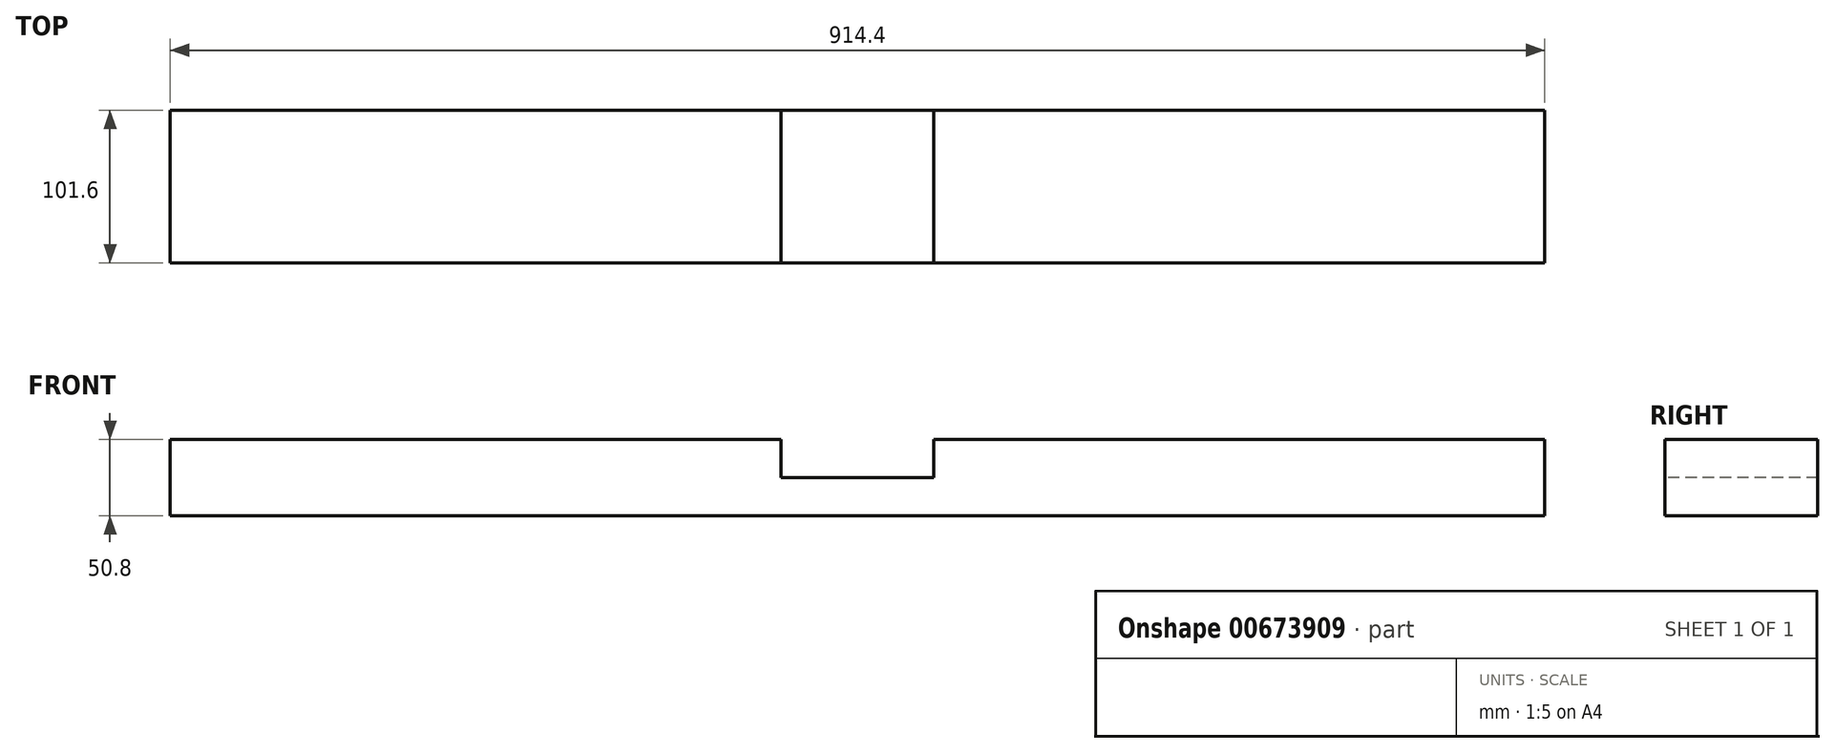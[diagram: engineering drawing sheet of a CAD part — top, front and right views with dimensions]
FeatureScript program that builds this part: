
annotation { "Feature Type Name" : "Feature", "Feature Type Description" : "" }
export const myFeature = defineFeature(function(context is Context, id is Id, definition is map)
    precondition{}
    {
        {
            var Q0;
            Q0=qCreatedBy(makeId("Front.planeOp"),FACE);
            var sketch = newSketch(context, id + "F0", { "sketchPlane" : qUnion([Q0])});
            skLineSegment(sketch, "E0.bottom", {"start": v(457.2, 25.4) * mm, "end": v(-457.2, 25.4) * mm});
            skLineSegment(sketch, "E0.top", {"start": v(457.2, -25.4) * mm, "end": v(-457.2, -25.4) * mm});
            skLineSegment(sketch, "E0.left", {"start": v(457.2, 25.4) * mm, "end": v(457.2, -25.4) * mm});
            skLineSegment(sketch, "E0.right", {"start": v(-457.2, 25.4) * mm, "end": v(-457.2, -25.4) * mm});
            skPoint(sketch, "E0.middle", {"position": v(0, 0) * mm});
            skSolve(sketch);
        }
        {
            var Q0;
            Q0 = qSketchRegion(id + "F0", true);
            extrude(context, id + "F1", {"entities" : qUnion([Q0]), "endBound" : BoundingType.SYMMETRIC, "depth" : 101.6 * mm, "offsetDistance" : 25.4 * mm});
        }
        {
            var Q0;
            Q0=makeQuery(id+"F1.opExtrude","SWEPT_FACE",FACE,{"disambiguationData":[OSD([sQuery(id+"F0.wireOp",EDGE,"E0.bottom")])]});
            var sketch = newSketch(context, id + "F2", { "sketchPlane" : qUnion([Q0])});
            skLineSegment(sketch, "E1.bottom", {"start": v(50.8, 50.8) * mm, "end": v(-50.8, 50.8) * mm});
            skLineSegment(sketch, "E1.top", {"start": v(50.8, -50.8) * mm, "end": v(-50.8, -50.8) * mm});
            skLineSegment(sketch, "E1.left", {"start": v(50.8, 50.8) * mm, "end": v(50.8, -50.8) * mm});
            skLineSegment(sketch, "E1.right", {"start": v(-50.8, 50.8) * mm, "end": v(-50.8, -50.8) * mm});
            skPoint(sketch, "E1.middle", {"position": v(0, 0) * mm});
            skSolve(sketch);
        }
        {
            var Q0;
            Q0 = qSketchRegion(id + "F2", true);
            extrude(context, id + "F3", {"entities" : qUnion([Q0]), "operationType" : NewBodyOperationType.REMOVE, "depth" : -25.4 * mm, "offsetDistance" : 25.4 * mm});
        }
    });
